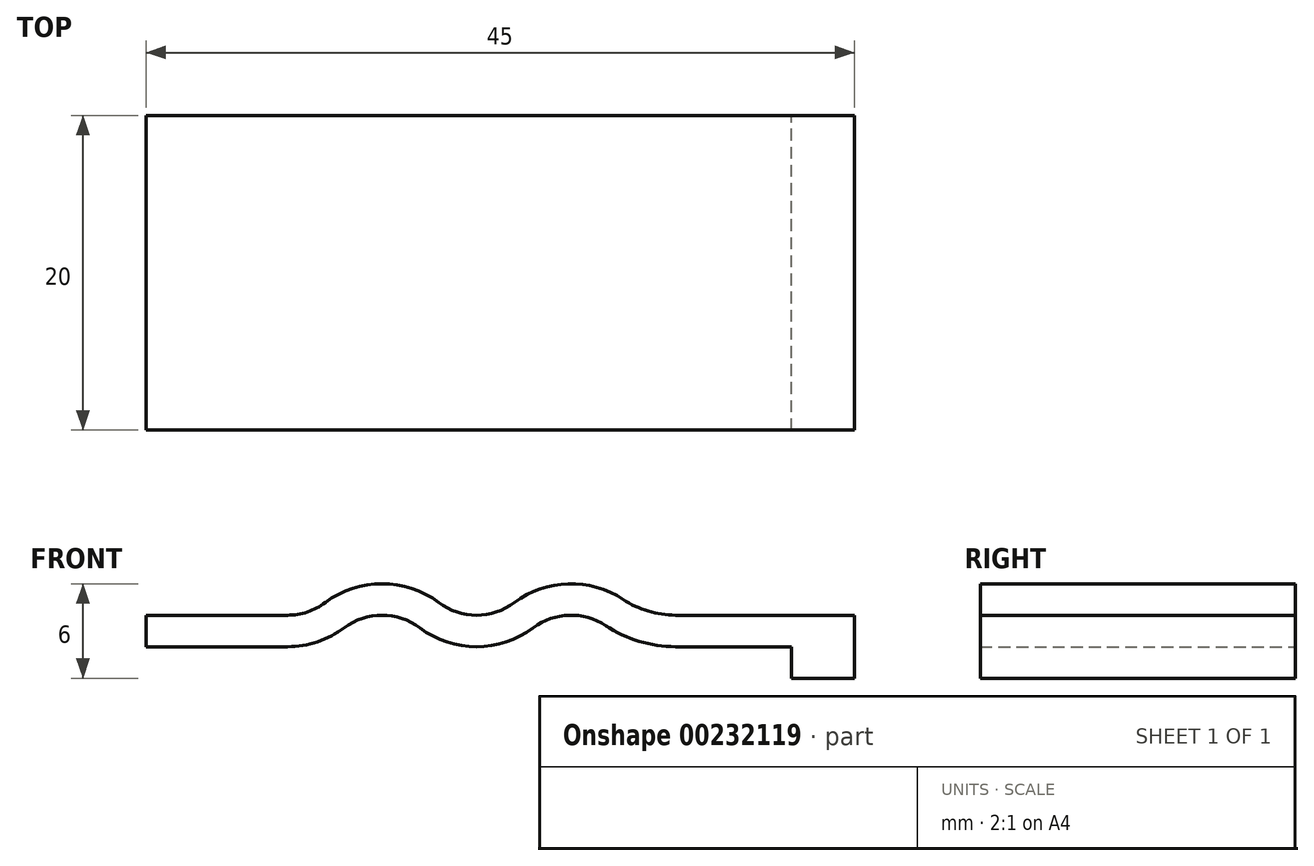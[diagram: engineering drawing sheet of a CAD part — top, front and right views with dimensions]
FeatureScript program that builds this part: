
annotation { "Feature Type Name" : "Feature", "Feature Type Description" : "" }
export const myFeature = defineFeature(function(context is Context, id is Id, definition is map)
    precondition{}
    {
        {
            var Q0;
            Q0=qCreatedBy(makeId("Front.planeOp"),FACE);
            var sketch = newSketch(context, id + "F0", { "sketchPlane" : qUnion([Q0])});
            skLineSegment(sketch, "E0", {"start": v(-45, 4) * mm, "end": v(-36, 4) * mm});
            skArc(sketch, "E1", {"start": v(-36, 4) * mm, "mid": v(-34.74, 4.2) * mm, "end": v(-33.6, 4.8) * mm});
            skArc(sketch, "E2", {"start": v(-33.6, 4.8) * mm, "mid": v(-30, 6) * mm, "end": v(-26.4, 4.8) * mm});
            skArc(sketch, "E3", {"start": v(-26.4, 4.8) * mm, "mid": v(-24, 4) * mm, "end": v(-21.6, 4.8) * mm});
            skArc(sketch, "E4", {"start": v(-21.6, 4.8) * mm, "mid": v(-18.17, 6) * mm, "end": v(-14.68, 5) * mm});
            skLineSegment(sketch, "E5", {"start": v(-13.53, 4) * mm, "end": v(-13.53, 4) * mm});
            skLineSegment(sketch, "E6", {"start": v(-11.37, 4) * mm, "end": v(0, 4) * mm});
            skLineSegment(sketch, "E7", {"start": v(-11.37, 4) * mm, "end": v(125.58, 4) * mm, "construction": true});
            skArc(sketch, "E8.filletArc", {"start": v(-14.68, 5) * mm, "mid": v(-13.1, 4.26) * mm, "end": v(-11.37, 4) * mm});
            skLineSegment(sketch, "E9", {"start": v(-115.92, 6) * mm, "end": v(124.58, 6) * mm, "construction": true});
            skLineSegment(sketch, "E10.0", {"start": v(-11.37, 2) * mm, "end": v(-4, 2) * mm});
            skArc(sketch, "E10.1", {"start": v(-15.79, 3.33) * mm, "mid": v(-13.68, 2.34) * mm, "end": v(-11.37, 2) * mm});
            skArc(sketch, "E10.2", {"start": v(-20.4, 3.2) * mm, "mid": v(-18.12, 4) * mm, "end": v(-15.79, 3.33) * mm});
            skLineSegment(sketch, "E10.3", {"start": v(-45, 2) * mm, "end": v(-36, 2) * mm});
            skArc(sketch, "E10.4", {"start": v(-36, 2) * mm, "mid": v(-34.1, 2.3) * mm, "end": v(-32.4, 3.2) * mm});
            skArc(sketch, "E10.5", {"start": v(-32.4, 3.2) * mm, "mid": v(-30, 4) * mm, "end": v(-27.6, 3.2) * mm});
            skArc(sketch, "E10.6", {"start": v(-27.6, 3.2) * mm, "mid": v(-24, 2) * mm, "end": v(-20.4, 3.2) * mm});
            skLineSegment(sketch, "E11", {"start": v(-45, 4) * mm, "end": v(-45, 2) * mm});
            skLineSegment(sketch, "E12.bottom", {"start": v(0, 4) * mm, "end": v(-4, 4) * mm});
            skLineSegment(sketch, "E12.top", {"start": v(0, 0) * mm, "end": v(-4, 0) * mm});
            skLineSegment(sketch, "E12.left", {"start": v(0, 4) * mm, "end": v(0, 0) * mm});
            skLineSegment(sketch, "E12.right", {"start": v(-4, 2) * mm, "end": v(-4, 0) * mm});
            skSolve(sketch);
        }
        {
            var Q0;
            Q0=makeQuery(id+"F0.imprint","IMPRINT",FACE,{"disambiguationData":[TD([[makeQuery(id+"F0.imprint","IMPRINT",EDGE,{"derivedFrom":sQuery(id+"F0.wireOp",EDGE,"E0")}),-1.0]])]});
            extrude(context, id + "F1", {"entities" : qUnion([Q0]), "depth" : 20 * mm});
        }
    });
